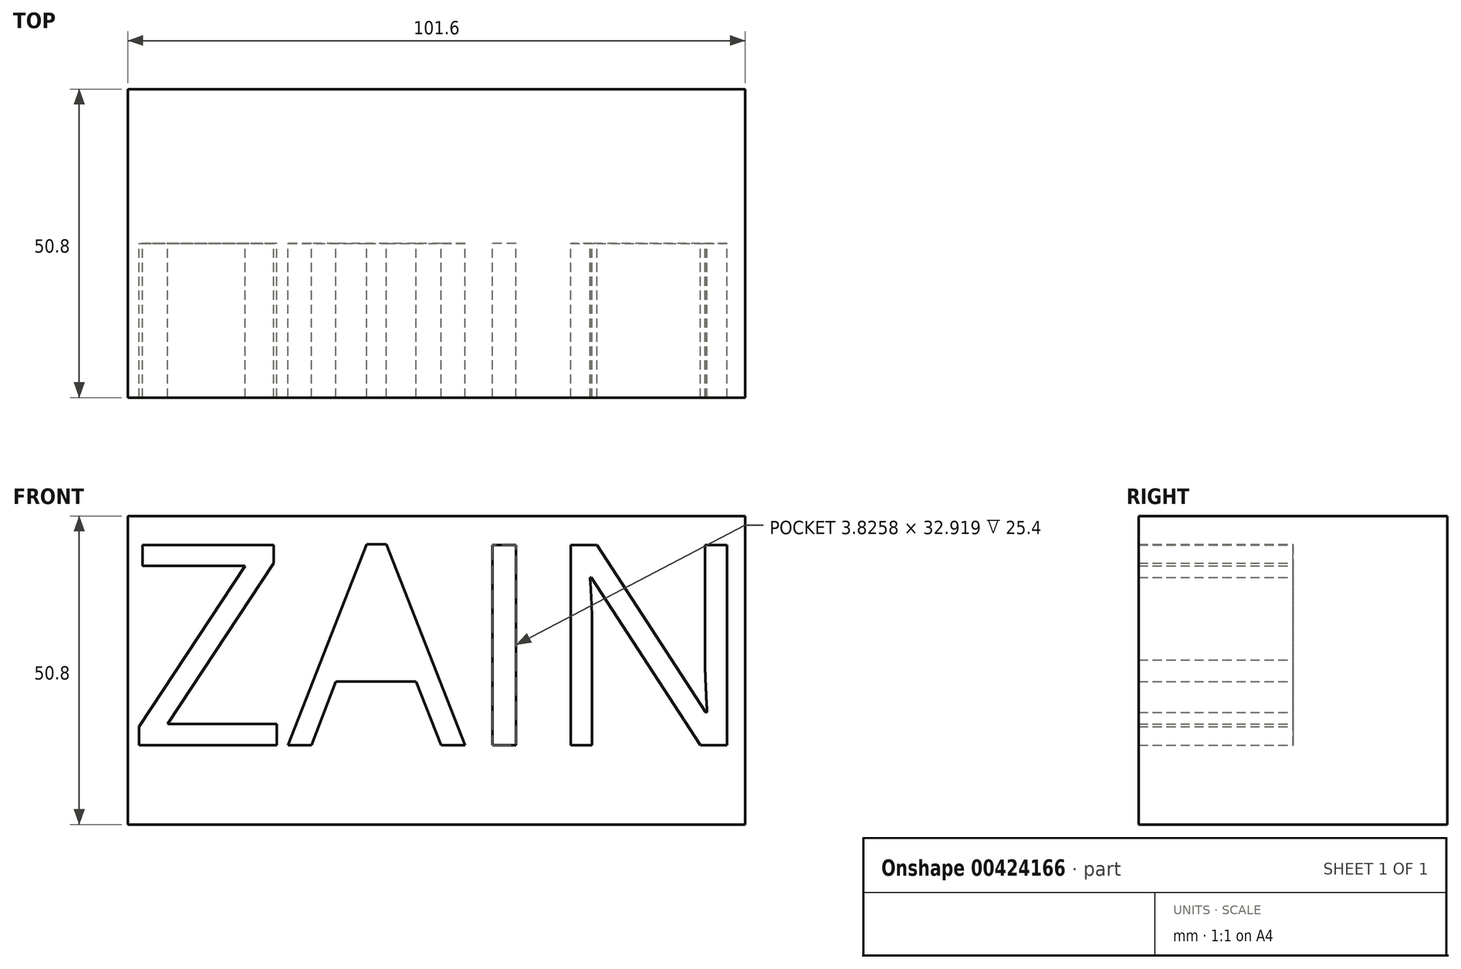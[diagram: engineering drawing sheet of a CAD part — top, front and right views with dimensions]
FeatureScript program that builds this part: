
annotation { "Feature Type Name" : "Feature", "Feature Type Description" : "" }
export const myFeature = defineFeature(function(context is Context, id is Id, definition is map)
    precondition{}
    {
        {
            var Q0;
            Q0=qCreatedBy(makeId("Front.planeOp"),FACE);
            var sketch = newSketch(context, id + "F0", { "sketchPlane" : qUnion([Q0])});
            skLineSegment(sketch, "E0.bottom", {"start": v(-54.63, 32.92) * mm, "end": v(46.97, 32.92) * mm});
            skLineSegment(sketch, "E0.top", {"start": v(-54.63, -17.88) * mm, "end": v(46.97, -17.88) * mm});
            skLineSegment(sketch, "E0.left", {"start": v(-54.63, 32.92) * mm, "end": v(-54.63, -17.88) * mm});
            skLineSegment(sketch, "E0.right", {"start": v(46.97, 32.92) * mm, "end": v(46.97, -17.88) * mm});
            skSolve(sketch);
        }
        {
            var Q0;
            Q0 = qSketchRegion(id + "F0", true);
            extrude(context, id + "F1", {"entities" : qUnion([Q0]), "depth" : 25.4 * mm});
        }
        {
            var Q0;
            Q0=makeQuery(id+"F1.opExtrude","CAP_FACE",FACE,{"disambiguationData":[OSD([sQuery(id+"F0.wireOp",EDGE,"E0.bottom"),sQuery(id+"F0.wireOp",EDGE,"E0.top"),sQuery(id+"F0.wireOp",EDGE,"E0.left"),sQuery(id+"F0.wireOp",EDGE,"E0.right")])],"isStart":false});
            var sketch = newSketch(context, id + "F2", { "sketchPlane" : qUnion([Q0])});
            skText(sketch, "E1", { "text": "ZAIN\n", "fontName": "OpenSans-Regular.ttf"});
            const initialGuessF2  = {"E1": [-0.05463, -0.0048, 1, 0, 0.0332]};
            skSetInitialGuess(sketch, initialGuessF2);
            skSolve(sketch);
        }
        {
            var Q0;
            Q0=makeQuery(id+"F2.imprint","IMPRINT",FACE,{"disambiguationData":[TD([[makeQuery(id+"F2.imprint","IMPRINT",EDGE,{"derivedFrom":sQuery(id+"F2.wireOp",EDGE,"E1.sketch_text.stroke-0")}),1.0]])]});
            extrude(context, id + "F3", {"entities" : qUnion([Q0]), "operationType" : NewBodyOperationType.ADD, "depth" : 25.4 * mm});
        }
    });
